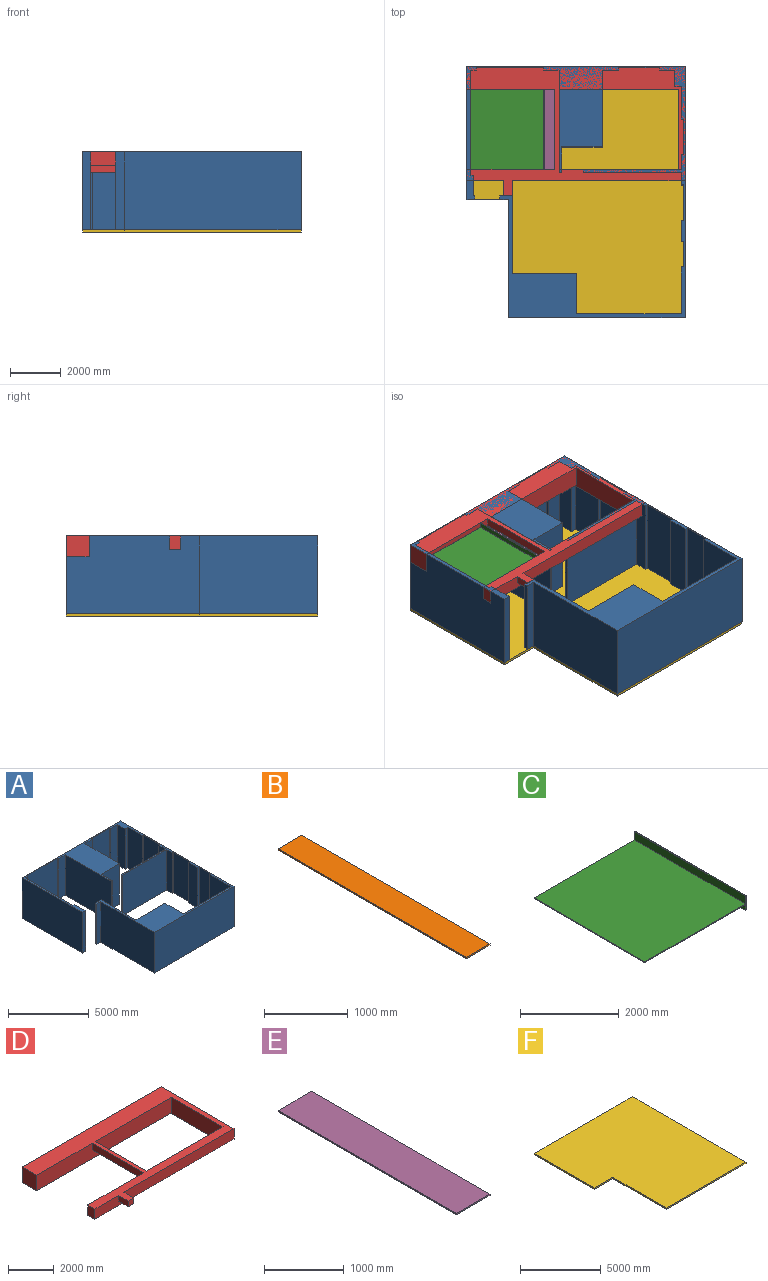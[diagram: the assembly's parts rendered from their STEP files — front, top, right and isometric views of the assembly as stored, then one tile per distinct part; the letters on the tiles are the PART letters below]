
ASSEMBLY  parts=6 mates=7
PART A: 54 faces, bbox 8600x9910x3060 mm
  f0: plane 3060x40mm, normal (0,1,0), area 122400mm2, adj f1,f51,f52,f53
  f1: plane 3060x810mm, normal (1,0,0), area 2478600mm2, adj f0,f2,f52,f53
  f2: plane 3060x110mm, normal (0,1,0), area 336600mm2, adj f1,f3,f52,f53
  f3: plane 4140x3060mm, normal (1,0,0), area 12668400mm2, adj f2,f4,f52,f53
  f4: plane 3060x220mm, normal (0,-1,0), area 673200mm2, adj f3,f5,f52,f53
  f5: plane 3060x100mm, normal (1,0,0), area 306000mm2, adj f4,f6,f52,f53
  f6: plane 3060x2650mm, normal (0,-1,0), area 8109000mm2, adj f5,f7,f52,f53
  f7: plane 3060x100mm, normal (-1,0,0), area 306000mm2, adj f6,f8,f52,f53
  f8: plane 3060x610mm, normal (0,-1,0), area 1866600mm2, adj f7,f9,f52,f53
  f9: plane 4030x3060mm, normal (-1,0,0), area 12331800mm2, adj f8,f10,f52,f53
  f10: plane 3060x100mm, normal (0,-1,0), area 306000mm2, adj f9,f11,f52,f53
  f11: plane 3060x1000mm, normal (1,0,0), area 3060000mm2, adj f10,f12,f52,f53
  f12: plane 3060x1600mm, normal (0,-1,0), area 4896000mm2, adj f11,f13,f52,f53
  f13: plane 3060x3030mm, normal (1,0,0), area 9271800mm2, adj f12,f14,f52,f53
  f14: plane 3060x650mm, normal (0,-1,0), area 1989000mm2, adj f13,f15,f52,f53
  f15: plane 3060x100mm, normal (1,0,0), area 306000mm2, adj f14,f16,f52,f53
  f16: plane 3060x1600mm, normal (0,-1,0), area 4896000mm2, adj f15,f17,f52,f53
  f17: plane 3060x100mm, normal (-1,0,0), area 306000mm2, adj f16,f18,f52,f53
  f18: plane 3060x620mm, normal (0,-1,0), area 1897200mm2, adj f17,f19,f52,f53
  f19: plane 3060x650mm, normal (-1,0,0), area 1989000mm2, adj f18,f20,f52,f53
  f20: plane 3060x250mm, normal (0,-1,0), area 765000mm2, adj f19,f21,f52,f53
  f21: plane 3060x1280mm, normal (-1,0,0), area 3916800mm2, adj f20,f22,f52,f53
  f22: plane 3060x100mm, normal (0,-1,0), area 306000mm2, adj f21,f23,f52,f53
  f23: plane 3060x1400mm, normal (-1,0,0), area 4284000mm2, adj f22,f24,f52,f53
  f24: plane 3060x100mm, normal (0,1,0), area 306000mm2, adj f23,f25,f52,f53
  f25: plane 3060x600mm, normal (-1,0,0), area 1836000mm2, adj f24,f26,f52,f53
  f26: plane 3870x3060mm, normal (0,1,0), area 11842200mm2, adj f25,f27,f52,f53
  f27: plane 3060x100mm, normal (-1,0,0), area 306000mm2, adj f26,f28,f52,f53
  f28: plane 3870x3060mm, normal (0,-1,0), area 11842200mm2, adj f27,f29,f52,f53
  f29: plane 3060x500mm, normal (-1,0,0), area 1530000mm2, adj f28,f30,f52,f53
  f30: plane 3060x100mm, normal (0,-1,0), area 306000mm2, adj f29,f31,f52,f53
  f31: plane 3060x1400mm, normal (-1,0,0), area 4284000mm2, adj f30,f32,f52,f53
  f32: plane 3060x100mm, normal (0,1,0), area 306000mm2, adj f31,f33,f52,f53
  f33: plane 3060x830mm, normal (-1,0,0), area 2539800mm2, adj f32,f34,f52,f53
  f34: plane 3060x100mm, normal (0,-1,0), area 306000mm2, adj f33,f35,f52,f53
  f35: plane 3060x1000mm, normal (-1,0,0), area 3060000mm2, adj f34,f36,f52,f53
  f36: plane 3060x100mm, normal (0,1,0), area 306000mm2, adj f35,f37,f52,f53
  f37: plane 3060x1850mm, normal (-1,0,0), area 5661000mm2, adj f36,f38,f52,f53
  f38: plane 4130x3060mm, normal (0,1,0), area 12637800mm2, adj f37,f39,f52,f53
  f39: plane 3060x1600mm, normal (1,0,0), area 4896000mm2, adj f38,f40,f52,f53
  f40: plane 3060x2530mm, normal (0,1,0), area 7741800mm2, adj f39,f41,f52,f53
  f41: plane 3060x3050mm, normal (1,0,0), area 9333000mm2, adj f40,f42,f52,f53
  f42: plane 3060x500mm, normal (0,1,0), area 1530000mm2, adj f41,f43,f52,f53
  f43: plane 3060x140mm, normal (-1,0,0), area 428400mm2, adj f42,f44,f52,f53
  f44: plane 3060x350mm, normal (0,-1,0), area 1071000mm2, adj f43,f45,f52,f53
  f45: plane 4660x3060mm, normal (-1,0,0), area 14259600mm2, adj f44,f46,f52,f53
  f46: plane 6960x3060mm, normal (0,-1,0), area 21297600mm2, adj f45,f47,f52,f53
  f47: plane 9910x3060mm, normal (1,0,0), area 30324600mm2, adj f46,f48,f52,f53
  f48: plane 8600x3060mm, normal (0,1,0), area 26316000mm2, adj f47,f49,f52,f53
  f49: plane 5250x3060mm, normal (-1,0,0), area 16065000mm2, adj f48,f50,f52,f53
  f50: plane 3060x300mm, normal (0,-1,0), area 918000mm2, adj f49,f51,f52,f53
  f51: plane 3060x150mm, normal (1,0,0), area 459000mm2, adj f0,f50,f52,f53
  f52: plane 9910x8600mm, normal (0,0,1), area 14442100mm2, adj f0,f1,f2,f3,f4,f5,f6,f7
  f53: plane 9910x8600mm, normal (0,0,-1), area 14442100mm2, adj f0,f1,f2,f3,f4,f5,f6,f7
PART B: 6 faces, bbox 400x3170x20 mm
  f0: plane 3170x20mm, normal (-1,0,0), area 63400mm2, adj f1,f3,f4,f5
  f1: plane 400x20mm, normal (0,-1,0), area 8000mm2, adj f0,f2,f4,f5
  f2: plane 3170x20mm, normal (1,0,0), area 63400mm2, adj f1,f3,f4,f5
  f3: plane 400x20mm, normal (0,1,0), area 8000mm2, adj f0,f2,f4,f5
  f4: plane 3170x400mm, normal (0,0,1), area 1268000mm2, adj f0,f1,f2,f3
  f5: plane 3170x400mm, normal (0,0,-1), area 1268000mm2, adj f0,f1,f2,f3
PART C: 10 faces, bbox 2890x3170x360 mm
  f0: plane 3170x200mm, normal (-1,0,0), area 634000mm2, adj f1,f2,f4,f9
  f1: plane 3170x20mm, normal (0,0,1), area 63400mm2, adj f0,f2,f4,f6
  f2: plane 2890x360mm, normal (0,1,0), area 64600mm2, adj f0,f1,f3,f5,f6,f7,f8,f9
  f3: plane 3170x20mm, normal (0,0,-1), area 63400mm2, adj f2,f4,f5,f6
  f4: plane 2890x360mm, normal (0,-1,0), area 64600mm2, adj f0,f1,f3,f5,f6,f7,f8,f9
  f5: plane 3170x140mm, normal (-1,0,0), area 443800mm2, adj f2,f3,f4,f8
  f6: plane 3170x360mm, normal (1,0,0), area 1141200mm2, adj f1,f2,f3,f4
  f7: plane 3170x20mm, normal (-1,0,0), area 63400mm2, adj f2,f4,f8,f9
  f8: plane 3170x2870mm, normal (0,0,-1), area 9097900mm2, adj f2,f4,f5,f7
  f9: plane 3170x2870mm, normal (0,0,1), area 9097900mm2, adj f0,f2,f4,f7
PART D: 20 faces, bbox 8600x5110x880 mm
  f0: plane 8360x550mm, normal (0,1,0), area 4529600mm2, adj f1,f2,f3,f8,f9,f12,f18
  f1: plane 3170x360mm, normal (1,0,0), area 1141200mm2, adj f0,f3,f5,f8
  f2: plane 3170x360mm, normal (-1,0,0), area 1141200mm2, adj f0,f3,f5,f8
  f3: plane 3170x190mm, normal (0,0,-1), area 602300mm2, adj f0,f1,f2,f5
  f4: plane 900x830mm, normal (-1,0,0), area 747000mm2, adj f5,f6,f7,f8
  f5: plane 8360x830mm, normal (0,-1,0), area 6870400mm2, adj f1,f2,f3,f4,f7,f8,f18
  f6: plane 8600x880mm, normal (0,1,0), area 7150000mm2, adj f4,f7,f8,f11,f18,f19
  f7: plane 8360x900mm, normal (0,0,-1), area 7524000mm2, adj f4,f5,f6,f18
  f8: plane 8600x5110mm, normal (0,0,1), area 13085100mm2, adj f0,f1,f2,f4,f5,f6,f9,f10
  f9: plane 550x440mm, normal (-1,0,0), area 242000mm2, adj f0,f8,f10,f12
  f10: plane 8600x550mm, normal (0,-1,0), area 4629350mm2, adj f8,f9,f11,f12,f14,f15,f16
  f11: plane 4510x880mm, normal (1,0,0), area 3823600mm2, adj f6,f8,f10,f12,f17,f19
  f12: plane 8600x440mm, normal (0,0,-1), area 3784000mm2, adj f0,f9,f10,f11,f17
  f13: plane 330x305mm, normal (0,-1,0), area 100650mm2, adj f8,f14,f15,f16
  f14: plane 600x305mm, normal (1,0,0), area 183000mm2, adj f8,f10,f13,f16
  f15: plane 600x305mm, normal (-1,0,0), area 183000mm2, adj f8,f10,f13,f16
  f16: plane 600x330mm, normal (0,0,-1), area 198000mm2, adj f10,f13,f14,f15
  f17: plane 330x240mm, normal (0,-1,0), area 79200mm2, adj f11,f12,f18,f19
  f18: plane 4070x880mm, normal (-1,0,0), area 2834600mm2, adj f0,f5,f6,f7,f8,f17,f19
  f19: plane 4070x240mm, normal (0,0,-1), area 976800mm2, adj f6,f11,f17,f18
PART E: 6 faces, bbox 600x3170x20 mm
  f0: plane 3170x20mm, normal (-1,0,0), area 63400mm2, adj f1,f3,f4,f5
  f1: plane 600x20mm, normal (0,-1,0), area 12000mm2, adj f0,f2,f4,f5
  f2: plane 3170x20mm, normal (1,0,0), area 63400mm2, adj f1,f3,f4,f5
  f3: plane 600x20mm, normal (0,1,0), area 12000mm2, adj f0,f2,f4,f5
  f4: plane 3170x600mm, normal (0,0,1), area 1902000mm2, adj f0,f1,f2,f3
  f5: plane 3170x600mm, normal (0,0,-1), area 1902000mm2, adj f0,f1,f2,f3
PART F: 8 faces, bbox 8600x9910x100 mm
  f0: plane 5250x100mm, normal (-1,0,0), area 525000mm2, adj f1,f5,f6,f7
  f1: plane 1640x100mm, normal (0,-1,0), area 164000mm2, adj f0,f2,f6,f7
  f2: plane 4660x100mm, normal (-1,0,0), area 466000mm2, adj f1,f3,f6,f7
  f3: plane 6960x100mm, normal (0,-1,0), area 696000mm2, adj f2,f4,f6,f7
  f4: plane 9910x100mm, normal (1,0,0), area 991000mm2, adj f3,f5,f6,f7
  f5: plane 8600x100mm, normal (0,1,0), area 860000mm2, adj f0,f4,f6,f7
  f6: plane 9910x8600mm, normal (0,0,-1), area 77583600mm2, adj f0,f1,f2,f3,f4,f5
  f7: plane 9910x8600mm, normal (0,0,1), area 77583600mm2, adj f0,f1,f2,f3,f4,f5
PLACE A t=(-2852.8,-413.58,100)mm
PLACE B t=(-2852.8,-413.58,100)mm
PLACE C t=(-2852.8,-413.58,100)mm
PLACE D t=(-2852.8,-413.58,100)mm
PLACE E t=(-2852.8,-413.58,100)mm
PLACE F t=(-2852.8,-413.58,100)mm
MATE planar D.f8 <-> C.f1  axis (0,0,1) through (-175.45,2857.99,3160)mm
MATE fastened A.f52 <-> D.f8  axis (0,0,1) through (-4642.8,4696.42,3160)mm
MATE fastened E.f5 <-> D.f3  axis (0,0,-1) through (-1202.8,2211.42,2800)mm
MATE fastened B.f5 <-> C.f3  axis (0,0,-1) through (-4492.8,2211.42,2800)mm
MATE fastened F.f7 <-> A.f53  axis (0,0,1) through (-3002.8,-5213.58,100)mm
MATE planar C.f2 <-> D.f5  axis (0,1,0) through (-2896.75,3796.42,2953.34)mm
MATE planar A.f3 <-> C.f7  axis (1,0,0) through (-4492.8,2476.42,1630)mm
